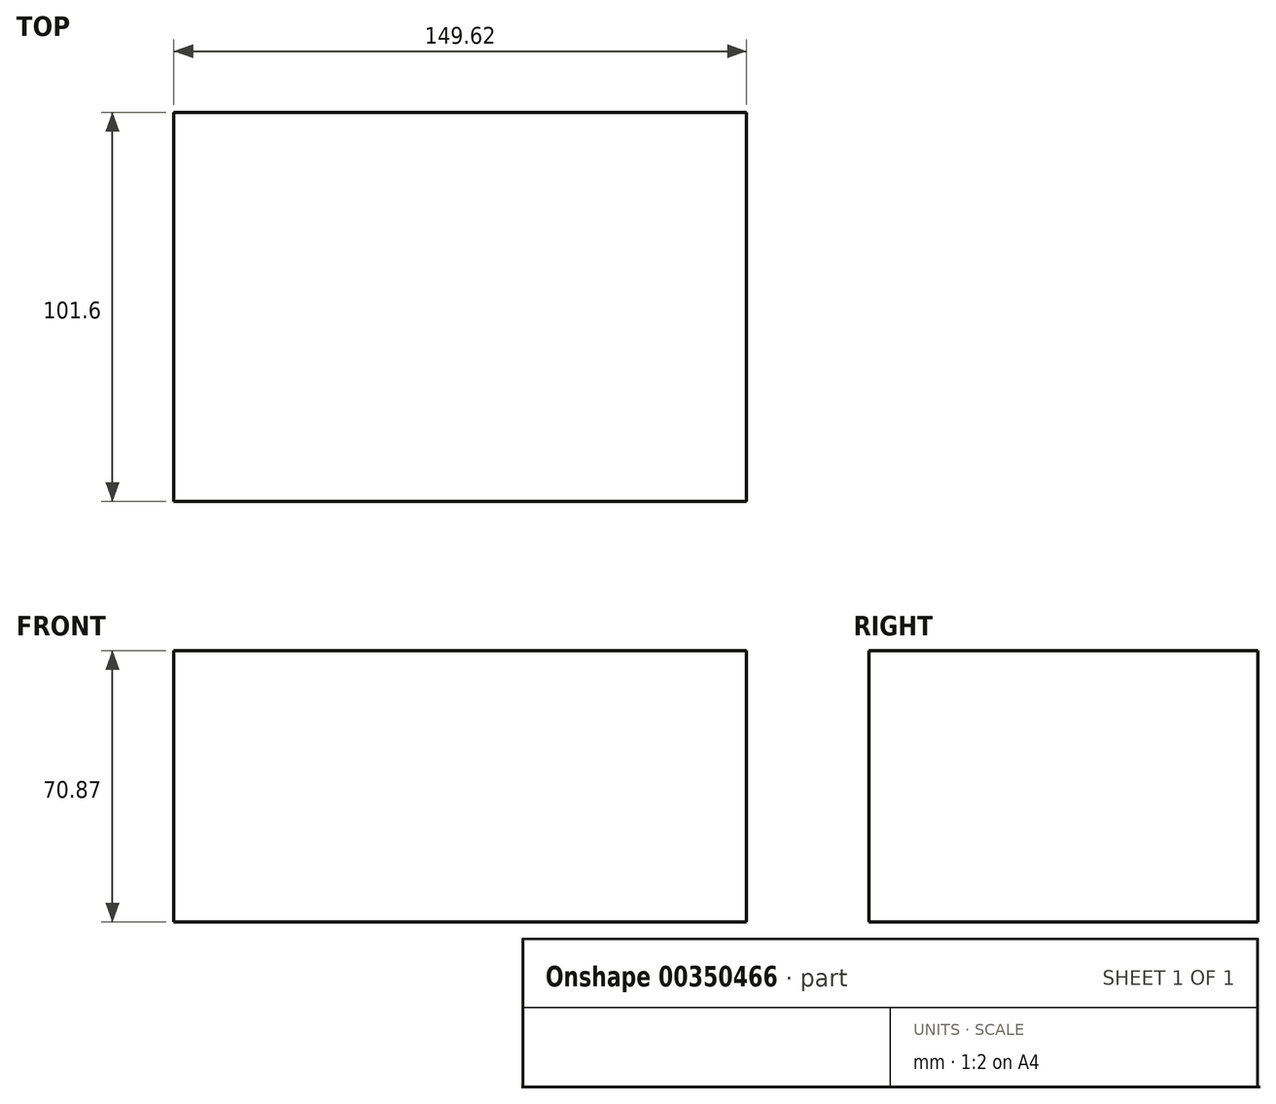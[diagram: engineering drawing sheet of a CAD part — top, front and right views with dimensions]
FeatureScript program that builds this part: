
annotation { "Feature Type Name" : "Feature", "Feature Type Description" : "" }
export const myFeature = defineFeature(function(context is Context, id is Id, definition is map)
    precondition{}
    {
        {
            var Q0;
            Q0=qCreatedBy(makeId("Top.planeOp"),FACE);
            var sketch = newSketch(context, id + "F0", { "sketchPlane" : qUnion([Q0])});
            skLineSegment(sketch, "E0.bottom", {"start": v(-73.18, 69.58) * mm, "end": v(76.44, 69.58) * mm});
            skLineSegment(sketch, "E0.top", {"start": v(-73.18, -32.02) * mm, "end": v(76.44, -32.02) * mm});
            skLineSegment(sketch, "E0.left", {"start": v(-73.18, 69.58) * mm, "end": v(-73.18, -32.02) * mm});
            skLineSegment(sketch, "E0.right", {"start": v(76.44, 69.58) * mm, "end": v(76.44, -32.02) * mm});
            skSolve(sketch);
        }
        {
            var Q0;
            Q0 = qSketchRegion(id + "F0", true);
            extrude(context, id + "F1", {"entities" : qUnion([Q0]), "depth" : 70.87 * mm});
        }
    });
